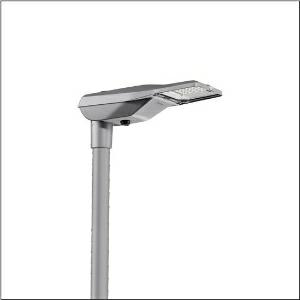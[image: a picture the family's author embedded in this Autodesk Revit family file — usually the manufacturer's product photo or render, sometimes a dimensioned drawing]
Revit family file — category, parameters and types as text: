
# Revit family: streetlight_sl_21_iq_micro___st1_0ab_5xe1m31u08cb_f63b
name_source: partatom
category: Lighting Fixtures
units: mm (PartAtom-declared; Revit-internal decimal feet)

## family parameters
Cut with Voids When Loaded = No
Host = Face
Light Source = No
Part Type = Normal
Room Calculation Point = No
Round Connector Dimension = Use Diameter
Shared = No

## types (1)
- --- (1 x LED, 2530 lm, 19.1 W, 3000K)
    Apparent Load = 19 VA
    CIE Flux Codes = 38 73 97 100 100
    Color Rendering = 70
    Color Temperature = 3000K
    Default Elevation = 1800 mm
    Description = Streetlight SL 21 iQ micro, mast luminaire, primary light control with lens, of PMMA, primary optical cover: cover, of toughened safety glass, transparent, light distribution: ST1.0aB, light emission: direct distribution, primary light characteristic: asymmetric, installation type: post-top, side-entry, LED, High Power LED, rated luminous flux: 2.530lm, luminous efficacy: 133lm/W, light colour: 730, colour temperature: 3000K, control gear: iQ-Street Remote, D4i with power reduction, control: pre-setting: logarithmic dimming characteristic, Street-Remote, Auto-Match, Temp-Guard, Lumen-Switch, Night-Set, Smart-Wire, Light-Fading, Desk-Remote (wireless, voltage-free reading and setting of iQ features in the workshop via application-optimized NFC function/RFID function), optimised constant luminous flux control (CLO 2.0), mains connection: 220..240V, AC, 50/60Hz, start of lifetime: 19W, end of service life: 20W, reduction: 9W, luminaire housing, of diecast aluminium, powder-coated, SITECO metallic grey (DB 702S), corrosivity category C5 high according to DIN EN ISO 12944, please order mast flange separately, inclination adjustable: 0°, 5°, 10°, 15°, sealing non-destructively replaceable, multi-level sealing system, length: 528mm, width: 235mm, height: 110mm, mast flange for spigot size: 42mm (side-entry): 5XC10008XM4, 60/48mm (side-entry/post-top): 5XC10108XM2, 76/60mm (side-entry/post-top): 5XC10108XM1, mounting height: 4..8m, Smart Interface below, protection rating (complete): IP66, insulation class (complete): insulation class II (safety insulation), certification: CE, ENEC, ENEC+, VDE, impact resistance: IK10, permissible operating ambient temperature for outdoor applications: -40..+50°C, standard-compliant lighting for roads and squares, packaging unit: 1 piece

Light Distribution: ST1.0aB
    Height = 110 mm
    Lamp = 1 x LED
    Lamp Light Flux = 2530 lm
    Lamp Power = 19.1 W
    Lamp count = 1
    Length = 528 mm
    Luminous efficacy = 132 lm/W
    Manufacturer = Siteco
    ModVariant = No
    Model = 5XE1M31U08CB
    Number of Poles = 1
    OnlyDefault = Yes
    Power Factor = 1
    Product Name = Streetlight SL 21 iQ micro | ST1.0aB
    Product group = mast luminaire | pylon top
    ProductGroupID = 6100
    Protection Class = Protection class II
    Protection Degree = IP 66
    RLX_Detail_Level = 1
    RLX_Emergency_Light_Flux = 0 lm
    RLX_Emergency_Type = 0
    RLX_Emergency_Type_DB = No
    RlxData = <blob elided: 99189 chars, md5=1633e082>
    Socket = socket
    Standby Power = 0 W
    System Light Flux = 2530 lm
    System Power = 19 W
    Type Comments = factory setting: luminous flux: 100 % | dim-lin: 254 | 387 mA
    Type Image = l_1277290.jpg
    URL = http://relux.com
    VarID = @adj_112815
    Voltage = 0 V
    Weight = 0.00 kg
    Width = 235 mm

## geometry (parser evidence)
native form markers: Blend x4, Sweep x10
no freeform markers — native parametric forms only
